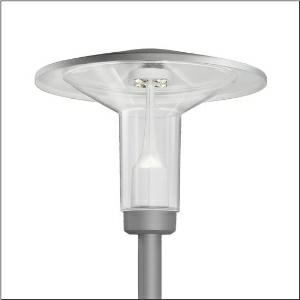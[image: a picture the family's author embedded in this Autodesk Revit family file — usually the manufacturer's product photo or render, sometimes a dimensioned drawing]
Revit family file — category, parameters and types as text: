
# Revit family: laterne_iq___pl1_2s_5xa5255jf14h000022_e294
name_source: partatom
category: Lighting Fixtures
units: mm (PartAtom-declared; Revit-internal decimal feet)

## family parameters
Cut with Voids When Loaded = No
Host = Face
Light Source = No
Part Type = Normal
Room Calculation Point = No
Round Connector Dimension = Use Diameter
Shared = No

## types (1)
- --- (1 x LED, 2970 lm, 19.3 W, 3000K)
    Apparent Load = 19 VA
    CIE Flux Codes = 25 63 94 98 100
    Color Rendering = 70
    Color Temperature = 3000K
    Default Elevation = 1800 mm
    Description = Lantern iQ, mast luminaire, Module 540 iQ-SR, primary light control with 3 zone facetted reflector, of plastic, silver coated, highly specular, structured, primary optical cover: cover, of PMMA, transparent, light distribution: PL1.2s, light emission: direct distribution, primary light characteristic: symmetric, installation type: post-top, LED, High Power LED, rated luminous flux: 2.970lm, luminous efficacy: 154lm/W, light colour: 730, colour temperature: 3000K, control gear: iQ Street-Remote, control: Street-Remote, Auto-Match, Temp-Guard, Lumen-Switch, Night-Set, Smart-Wire, Light-Fading, Desk-Remote (wireless, voltage-free reading and setting of iQ features in the workshop via application-optimized NFC function/RFID function), optimised constant luminous flux control (CLO 2.0), pre-setting: logarithmic dimming characteristic, mains connection: 230..240V, AC, 50/60Hz, connection cable pre-assembled, cable length: 5,5m, wiring characteristics: H07RN-F, start of lifetime: 19W, end of service life: 21W, reduction: 10W, luminaire housing, upper part, of glass-fibre reinforced polyester, coated, Siteco® metallic grey (DB 702S), diameter: 750mm, height: 583mm, spigot size: d x l = 76 x 70mm (post-top) | with reducer (optional accessory) 60 x 70mm, mounting height: 3..5m, post-top mast mounting element, of diecast aluminium, coated, Siteco® metallic grey (DB 702S), Module 540 iQ-SR, traffic white (RAL 9016), equipment: standard, protection rating (complete): IP65, insulation class (complete): insulation class II (safety insulation), certification: CE, ENEC, VDE, packaging unit: 1 piece

Light Distribution: PL1.2s
    Height = 583 mm
    Lamp = 1 x LED
    Lamp Light Flux = 2970 lm
    Lamp Power = 19.3 W
    Lamp count = 1
    Length = 750 mm
    Luminous efficacy = 154 lm/W
    Manufacturer = Siteco
    ModVariant = No
    Model = 5XA5255JF14H000022
    Number of Poles = 1
    OnlyDefault = Yes
    Power Factor = 1
    Product Name = Laterne iQ | PL1.2s
    Product group = mast luminaire | pylon top
    ProductGroupID = 6100
    Protection Class = Protection class II
    Protection Degree = IP 65
    RLX_Detail_Level = 1
    RLX_Emergency_Light_Flux = 0 lm
    RLX_Emergency_Type = 0
    RLX_Emergency_Type_DB = No
    RlxData = <blob elided: 31673 chars, md5=b3b0de6f>
    Socket = socket
    Standby Power = 0 W
    System Light Flux = 2970 lm
    System Power = 19 W
    Type Comments = factory setting: luminous flux: 100 % | dim-lin: 254 | 403 mA
    Type Image = l_1006050.jpg
    URL = http://relux.com
    VarID = @adj_145850
    Voltage = 0 V
    Weight = 0.00 kg
    Width = 0 mm  [stored 0 ft]

note: [stored X ft] marks values corroborated as IEEE doubles in the binary element streams (Revit-internal decimal feet)

## geometry (parser evidence)
native form markers: Blend x4, Sweep x10
no freeform markers — native parametric forms only
